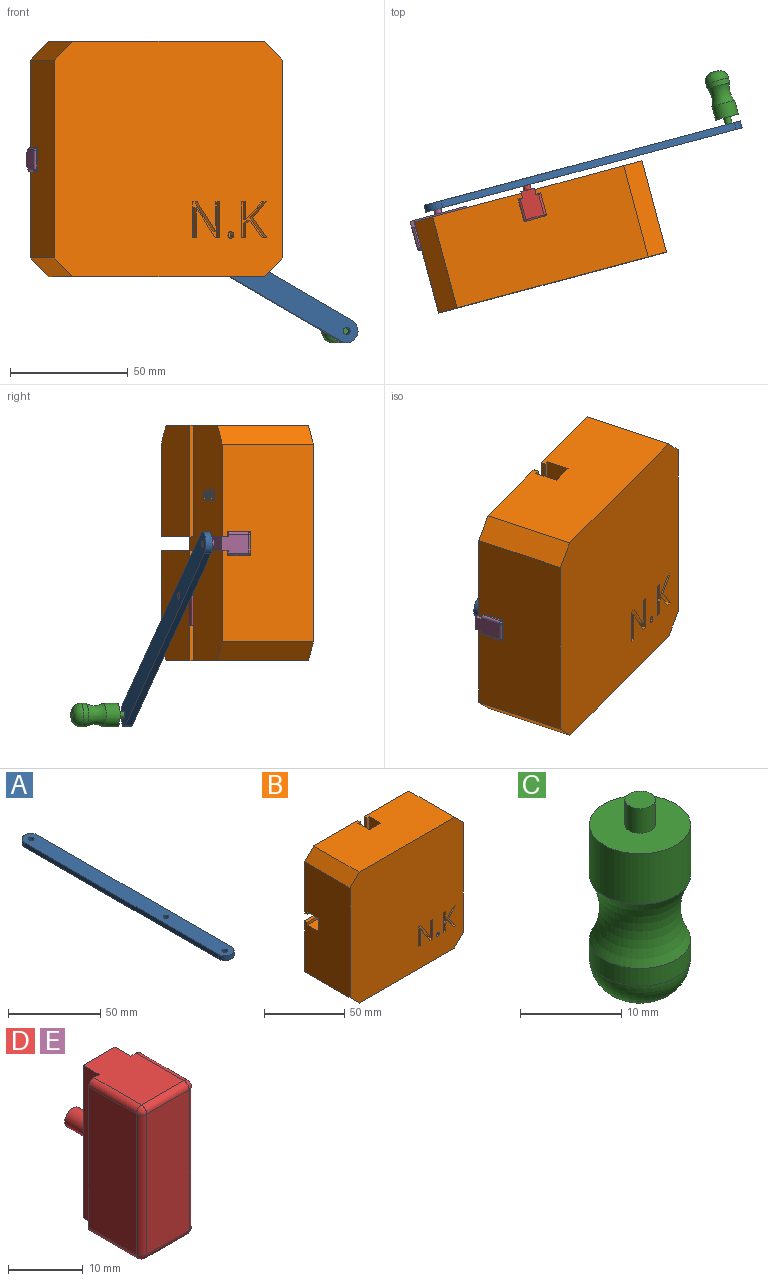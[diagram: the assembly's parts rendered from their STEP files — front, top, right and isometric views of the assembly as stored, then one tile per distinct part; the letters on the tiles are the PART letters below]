
ASSEMBLY  parts=5 mates=6
PART A: 9 faces, bbox 10x158x3 mm
  f0: cylinder r=5mm len=10mm, axis (0,0,-1), area 47.1mm2, adj f1,f6,f7,f8
  f1: plane 148x3mm, normal (-1,0,0), area 444mm2, adj f0,f2,f7,f8
  f2: cylinder r=5mm len=10mm, axis (0,0,-1), area 47.1mm2, adj f1,f6,f7,f8
  f3: cylinder r=1.5mm len=3mm, axis (0,0,-1), area 28.3mm2, adj f7,f8
  f4: cylinder r=1.5mm len=3mm, axis (0,0,-1), area 28.3mm2, adj f7,f8
  f5: cylinder r=1.5mm len=3mm, axis (0,0,-1), area 28.3mm2, adj f7,f8
  f6: plane 148x3mm, normal (1,0,0), area 444mm2, adj f0,f2,f7,f8
  f7: plane 158x10mm, normal (0,0,1), area 1537.3mm2, adj f0,f1,f2,f3,f4,f5,f6
  f8: plane 158x10mm, normal (0,0,-1), area 1537.3mm2, adj f0,f1,f2,f3,f4,f5,f6
PART B: 184 faces, bbox 100x40x100 mm
  f0: plane 47.23x46.91mm, normal (0,1,0), area 2152.4mm2, adj f13,f15,f18,f28,f36,f80,f81,f82
  f1: plane 100x100mm, normal (0,-1,0), area 9730.3mm2, adj f13,f14,f15,f16,f34,f35,f36,f37
  f2: plane 46.91x46.77mm, normal (0,1,0), area 2162.2mm2, adj f4,f14,f15,f27,f35
  f3: plane 47.09x46.77mm, normal (0,1,0), area 2170.2mm2, adj f12,f14,f16,f29,f34
  f4: plane 46.77x2mm, normal (1,0,0), area 93.5mm2, adj f2,f5,f14,f27
  f5: plane 46.77x1.91mm, normal (0,-1,0), area 89.5mm2, adj f4,f6,f14,f27
  f6: plane 46.77x10mm, normal (1,0,0), area 447.5mm2, adj f5,f14,f20,f23,f24,f27
  f7: plane 47.23x10mm, normal (1,0,0), area 453.4mm2, adj f8,f13,f19,f25,f26,f28
  f8: plane 45.3x10mm, normal (0,1,0), area 453mm2, adj f7,f10,f13,f25
  f9: plane 46.77x10mm, normal (-1,0,0), area 447.5mm2, adj f11,f14,f20,f24,f29,f30
  f10: plane 47.23x10mm, normal (-1,0,0), area 453.4mm2, adj f8,f13,f21,f25,f32,f33
  f11: plane 46.77x2.09mm, normal (0,-1,0), area 97.6mm2, adj f9,f12,f14,f29
  f12: plane 46.77x2mm, normal (-1,0,0), area 93.5mm2, adj f3,f11,f14,f29
  f13: plane 84x40mm, normal (0,0,1), area 3248mm2, adj f0,f1,f7,f8,f10,f17,f18,f19
  f14: plane 84x40mm, normal (0,0,-1), area 3248mm2, adj f1,f2,f3,f4,f5,f6,f9,f11
  f15: plane 84x40mm, normal (-1,0,0), area 3246.5mm2, adj f0,f1,f2,f23,f24,f25,f26,f27
  f16: plane 84x40mm, normal (1,0,0), area 3246.5mm2, adj f1,f3,f17,f24,f25,f29,f30,f31
  f17: plane 47.23x47.09mm, normal (0,1,0), area 2191.8mm2, adj f13,f16,f22,f33,f37
  f18: plane 47.23x2mm, normal (1,0,0), area 94.5mm2, adj f0,f13,f19,f28
  f19: plane 47.23x1.91mm, normal (0,-1,0), area 90.4mm2, adj f7,f13,f18,f28
  f20: plane 44.7x10mm, normal (0,1,0), area 447mm2, adj f6,f9,f14,f24
  f21: plane 47.23x2.09mm, normal (0,-1,0), area 98.5mm2, adj f10,f13,f22,f33
  f22: plane 47.23x2mm, normal (-1,0,0), area 94.5mm2, adj f13,f17,f21,f33
  f23: plane 45x2.07mm, normal (0,-1,0), area 93mm2, adj f6,f15,f24,f27
  f24: plane 100x10mm, normal (0,0,1), area 902.5mm2, adj f6,f9,f15,f16,f20,f23,f30,f31
  f25: plane 100x10mm, normal (0,0,-1), area 902.5mm2, adj f7,f8,f10,f15,f16,f26,f31,f32
  f26: plane 45x1.93mm, normal (0,-1,0), area 87mm2, adj f7,f15,f25,f28
  f27: plane 46.91x2.25mm, normal (0,0,1), area 104.9mm2, adj f2,f4,f5,f6,f15,f23
  f28: plane 46.91x2.25mm, normal (0,0,-1), area 104.9mm2, adj f0,f7,f15,f18,f19,f26
  f29: plane 47.09x2.25mm, normal (0,0,1), area 105.2mm2, adj f3,f9,f11,f12,f16,f30
  f30: plane 45x2.07mm, normal (0,-1,0), area 93mm2, adj f9,f16,f24,f29
  f31: plane 100x10mm, normal (0,1,0), area 1000mm2, adj f15,f16,f24,f25
  f32: plane 45x1.93mm, normal (0,-1,0), area 87mm2, adj f10,f16,f25,f33
  f33: plane 47.09x2.25mm, normal (0,0,-1), area 105.2mm2, adj f10,f16,f17,f21,f22,f32
  f34: plane 40x8mm, normal (0.71,0,-0.71), area 452.5mm2, adj f1,f3,f14,f16
  f35: plane 40x8mm, normal (-0.71,0,-0.71), area 452.5mm2, adj f1,f2,f14,f15
  f36: plane 40x8mm, normal (-0.71,0,0.71), area 452.5mm2, adj f0,f1,f13,f15
  f37: plane 40x8mm, normal (0.71,0,0.71), area 452.5mm2, adj f1,f13,f16,f17
  f38: plane 4.6x2.07mm, normal (0,0,1), area 9.5mm2, adj f1,f39,f49,f50
  f39: plane 8.56x6.31mm, normal (-0.8,0,-0.59), area 48.9mm2, adj f1,f38,f40,f50
  f40: plane 6.57x6.08mm, normal (-0.73,0,0.68), area 41.2mm2, adj f1,f39,f41,f50
  f41: plane 4.6x2.08mm, normal (0,0,-1), area 9.6mm2, adj f1,f40,f42,f50
  f42: plane 7.51x6.86mm, normal (0.74,0,-0.67), area 46.8mm2, adj f1,f41,f43,f50
  f43: plane 7.51x4.6mm, normal (-1,0,0), area 34.5mm2, adj f1,f42,f44,f50
  f44: plane 4.6x1.76mm, normal (0,0,-1), area 8.1mm2, adj f1,f43,f45,f50
  f45: plane 15.13x4.6mm, normal (1,0,0), area 69.6mm2, adj f1,f44,f46,f50
  f46: plane 4.6x1.76mm, normal (0,0,1), area 8.1mm2, adj f1,f45,f47,f50
  f47: plane 5.93x4.6mm, normal (-1,0,0), area 27.3mm2, adj f1,f46,f48,f50
  f48: plane 4.6x1.59mm, normal (-0.66,0,0.75), area 9.8mm2, adj f1,f47,f49,f50
  f49: plane 7.34x5.52mm, normal (0.8,0,0.6), area 42.2mm2, adj f1,f38,f48,f50
  f50: plane 15.13x10.93mm, normal (0,-1,0), area 60.4mm2, adj f38,f39,f40,f41,f42,f43,f44,f45
  f51: extruded ~4.6x1.05mm, area 5.2mm2, adj f1,f52,f58,f59
  f52: extruded ~4.6x1.07mm, area 5.3mm2, adj f1,f51,f53,f59
  f53: extruded ~4.6x0.88mm, area 4.4mm2, adj f1,f52,f54,f59
  f54: extruded ~4.6x0.93mm, area 4.7mm2, adj f1,f53,f55,f59
  f55: extruded ~4.6x1.04mm, area 5.1mm2, adj f1,f54,f56,f59
  f56: extruded ~4.6x1.05mm, area 5.2mm2, adj f1,f55,f57,f59
  f57: extruded ~4.6x0.94mm, area 4.7mm2, adj f1,f56,f58,f59
  f58: extruded ~4.6x0.91mm, area 4.6mm2, adj f1,f51,f57,f59
  f59: plane 2.81x2.49mm, normal (0,-1,0), area 5.8mm2, adj f51,f52,f53,f54,f55,f56,f57,f58
  f60: plane 4.6x2.01mm, normal (0,0,1), area 9.2mm2, adj f1,f61,f74,f75
  f61: plane 15.13x4.6mm, normal (-1,0,0), area 69.6mm2, adj f1,f60,f62,f75
  f62: plane 4.6x1.65mm, normal (0,0,-1), area 7.6mm2, adj f1,f61,f63,f75
  f63: plane 8.68x4.6mm, normal (1,0,0), area 39.9mm2, adj f1,f62,f64,f75
  f64: extruded ~4.6x2.17mm, area 10mm2, adj f1,f63,f65,f75
  f65: extruded ~4.6x1.8mm, area 8.3mm2, adj f1,f64,f66,f75
  f66: plane 4.6x0.08mm, normal (0,0,-1), area 0.4mm2, adj f1,f65,f67,f75
  f67: plane 12.65x8.25mm, normal (-0.84,0,-0.55), area 69.5mm2, adj f1,f66,f68,f75
  f68: plane 4.6x1.99mm, normal (0,0,-1), area 9.1mm2, adj f1,f67,f69,f75
  f69: plane 15.13x4.6mm, normal (1,0,0), area 69.6mm2, adj f1,f68,f70,f75
  f70: plane 4.6x1.63mm, normal (0,0,1), area 7.5mm2, adj f1,f69,f71,f75
  f71: plane 8.6x4.6mm, normal (-1,0,0), area 39.6mm2, adj f1,f70,f72,f75
  f72: extruded ~4.6x4.1mm, area 18.9mm2, adj f1,f71,f73,f75
  f73: plane 4.6x0.08mm, normal (0,0,1), area 0.4mm2, adj f1,f72,f74,f75
  f74: plane 12.7x8.27mm, normal (0.84,0,0.55), area 69.7mm2, adj f1,f60,f73,f75
  f75: plane 15.13x11.82mm, normal (0,-1,0), area 75.6mm2, adj f60,f61,f62,f63,f64,f65,f66,f67
  f76: extruded ~23.6x0.68mm, area 17.9mm2, adj f77,f94,f95,f182
  f77: extruded ~23.6x0.65mm, area 17.2mm2, adj f76,f78,f95,f182
  f78: extruded ~23.6x0.78mm, area 19.6mm2, adj f77,f79,f95,f182
  f79: plane 23.6x1.86mm, normal (0,0,-1), area 43.9mm2, adj f78,f94,f95,f182
  f80: extruded ~23.6x1.24mm, area 32.4mm2, adj f0,f81,f93,f95
  f81: extruded ~23.6x0.61mm, area 14.6mm2, adj f0,f80,f82,f95
  f82: extruded ~23.6x0.54mm, area 13.4mm2, adj f0,f81,f83,f95
  f83: plane 23.6x0.48mm, normal (1,0,0), area 11.3mm2, adj f0,f82,f84,f95
  f84: extruded ~23.6x1.14mm, area 27.6mm2, adj f0,f83,f85,f95
  f85: extruded ~23.6x0.85mm, area 22mm2, adj f0,f84,f86,f95
  f86: extruded ~23.6x0.95mm, area 24.2mm2, adj f0,f85,f87,f95
  f87: plane 23.6x2.45mm, normal (0,0,1), area 57.8mm2, adj f0,f86,f88,f95
  f88: plane 23.6x0.34mm, normal (1,0,0), area 8mm2, adj f0,f87,f89,f95
  f89: extruded ~23.6x1.16mm, area 29.6mm2, adj f0,f88,f90,f95
  f90: extruded ~23.6x1.06mm, area 27.9mm2, adj f0,f89,f91,f95
  f91: extruded ~23.6x1.14mm, area 30.4mm2, adj f0,f90,f92,f95
  f92: extruded ~23.6x1.37mm, area 34.5mm2, adj f0,f91,f93,f95
  f93: extruded ~23.6x1.33mm, area 34.1mm2, adj f0,f80,f92,f95
  f94: extruded ~23.6x0.77mm, area 19.9mm2, adj f76,f79,f95,f182
  f95: plane 3.69x3.01mm, normal (0,1,0), area 5mm2, adj f76,f77,f78,f79,f80,f81,f82,f83
  f96: plane 23.6x0.54mm, normal (0,0,1), area 12.7mm2, adj f0,f97,f99,f100
  f97: plane 23.6x5.05mm, normal (1,0,0), area 119.2mm2, adj f0,f96,f98,f100
  f98: plane 23.6x0.54mm, normal (0,0,-1), area 12.7mm2, adj f0,f97,f99,f100
  f99: plane 23.6x5.05mm, normal (-1,0,0), area 119.2mm2, adj f0,f96,f98,f100
  f100: plane 5.05x0.54mm, normal (0,1,0), area 2.7mm2, adj f96,f97,f98,f99
  f101: plane 23.6x2.3mm, normal (-1,0,0), area 54.3mm2, adj f0,f102,f118,f119
  f102: plane 23.6x0.54mm, normal (0,0,1), area 12.7mm2, adj f0,f101,f103,f119
  f103: plane 23.6x2.32mm, normal (1,0,0), area 54.7mm2, adj f0,f102,f104,f119
  f104: extruded ~23.6x0.99mm, area 25.2mm2, adj f0,f103,f105,f119
  f105: extruded ~23.6x0.98mm, area 24.8mm2, adj f0,f104,f106,f119
  f106: extruded ~23.6x0.67mm, area 16.3mm2, adj f0,f105,f107,f119
  f107: extruded ~23.6x0.45mm, area 14.5mm2, adj f0,f106,f108,f119
  f108: plane 23.6x0.03mm, normal (0,0,-1), area 0.8mm2, adj f0,f107,f109,f119
  f109: extruded ~23.6x0.46mm, area 10.8mm2, adj f0,f108,f110,f119
  f110: plane 23.6x1.53mm, normal (1,0,0), area 36.1mm2, adj f0,f109,f111,f119
  f111: plane 23.6x0.54mm, normal (0,0,-1), area 12.7mm2, adj f0,f110,f112,f119
  f112: plane 23.6x5.05mm, normal (-1,0,0), area 119.2mm2, adj f0,f111,f113,f119
  f113: plane 23.6x0.54mm, normal (0,0,1), area 12.7mm2, adj f0,f112,f114,f119
  f114: plane 23.6x1.86mm, normal (1,0,0), area 43.9mm2, adj f0,f113,f115,f119
  f115: extruded ~23.6x1mm, area 24.8mm2, adj f0,f114,f116,f119
  f116: extruded ~23.6x0.82mm, area 21.3mm2, adj f0,f115,f117,f119
  f117: extruded ~23.6x0.62mm, area 15.9mm2, adj f0,f116,f118,f119
  f118: extruded ~23.6x0.65mm, area 16.4mm2, adj f0,f101,f117,f119
  f119: plane 5.05x2.97mm, normal (0,1,0), area 5.4mm2, adj f101,f102,f103,f104,f105,f106,f107,f108
  f120: extruded ~23.6x0.52mm, area 15.8mm2, adj f0,f121,f134,f135
  f121: plane 23.6x0.03mm, normal (0,0,-1), area 0.6mm2, adj f0,f120,f122,f135
  f122: extruded ~23.6x0.55mm, area 13mm2, adj f0,f121,f123,f135
  f123: plane 23.6x2.68mm, normal (1,0,0), area 63.2mm2, adj f0,f122,f124,f135
  f124: plane 23.6x0.53mm, normal (0,0,-1), area 12.6mm2, adj f0,f123,f125,f135
  f125: plane 23.6x5.05mm, normal (-1,0,0), area 119.2mm2, adj f0,f124,f126,f135
  f126: plane 23.6x0.53mm, normal (0,0,1), area 12.6mm2, adj f0,f125,f127,f135
  f127: plane 23.6x1.33mm, normal (1,0,0), area 31.4mm2, adj f0,f126,f128,f135
  f128: plane 23.6x0.41mm, normal (0.65,0,0.76), area 12.6mm2, adj f0,f127,f129,f135
  f129: plane 23.6x1.68mm, normal (-0.8,0,0.6), area 49.5mm2, adj f0,f128,f130,f135
  f130: plane 23.6x0.65mm, normal (0,0,1), area 15.4mm2, adj f0,f129,f131,f135
  f131: plane 23.6x2.04mm, normal (0.8,0,-0.6), area 60.4mm2, adj f0,f130,f132,f135
  f132: plane 23.6x1.52mm, normal (0.72,0,0.69), area 49.3mm2, adj f0,f131,f133,f135
  f133: plane 23.6x0.64mm, normal (0,0,-1), area 15.1mm2, adj f0,f132,f134,f135
  f134: plane 23.6x1.22mm, normal (-0.73,0,-0.69), area 39.5mm2, adj f0,f120,f133,f135
  f135: plane 5.05x2.85mm, normal (0,1,0), area 5.1mm2, adj f120,f121,f122,f123,f124,f125,f126,f127
  f136: extruded ~23.6x0.79mm, area 20.3mm2, adj f137,f162,f163,f183
  f137: extruded ~23.6x0.49mm, area 12.5mm2, adj f136,f138,f163,f183
  f138: extruded ~23.6x0.45mm, area 11.7mm2, adj f137,f139,f163,f183
  f139: extruded ~23.6x0.55mm, area 15.3mm2, adj f138,f140,f163,f183
  f140: extruded ~23.6x0.93mm, area 22.6mm2, adj f139,f141,f163,f183
  f141: plane 23.6x0.54mm, normal (0.04,0,1), area 12.7mm2, adj f140,f142,f163,f183
  f142: plane 23.6x0.32mm, normal (-1,0,0), area 7.6mm2, adj f141,f162,f163,f183
  f143: plane 23.6x0.51mm, normal (-0.98,0,0.21), area 12.2mm2, adj f0,f144,f161,f163
  f144: plane 23.6x0.4mm, normal (0,0,1), area 9.4mm2, adj f0,f143,f145,f163
  f145: plane 23.6x2.43mm, normal (1,0,0), area 57.3mm2, adj f0,f144,f146,f163
  f146: extruded ~23.6x0.91mm, area 23.2mm2, adj f0,f145,f147,f163
  f147: extruded ~23.6x0.94mm, area 23.7mm2, adj f0,f146,f148,f163
  f148: extruded ~23.6x0.63mm, area 15mm2, adj f0,f147,f149,f163
  f149: extruded ~23.6x0.58mm, area 14.6mm2, adj f0,f148,f150,f163
  f150: plane 23.6x0.41mm, normal (-0.93,0,0.37), area 10.5mm2, adj f0,f149,f151,f163
  f151: extruded ~23.6x1.01mm, area 24.8mm2, adj f0,f150,f152,f163
  f152: extruded ~23.6x0.58mm, area 14.8mm2, adj f0,f151,f153,f163
  f153: extruded ~23.6x0.62mm, area 15.5mm2, adj f0,f152,f154,f163
  f154: plane 23.6x0.22mm, normal (-1,0,0), area 5.2mm2, adj f0,f153,f155,f163
  f155: plane 23.6x0.6mm, normal (-0.03,0,-1), area 14.2mm2, adj f0,f154,f156,f163
  f156: extruded ~23.6x1.72mm, area 54.6mm2, adj f0,f155,f157,f163
  f157: extruded ~23.6x0.78mm, area 20.2mm2, adj f0,f156,f158,f163
  f158: extruded ~23.6x0.83mm, area 21.1mm2, adj f0,f157,f159,f163
  f159: extruded ~23.6x0.66mm, area 16mm2, adj f0,f158,f160,f163
  f160: extruded ~23.6x0.53mm, area 16.6mm2, adj f0,f159,f161,f163
  f161: plane 23.6x0.03mm, normal (0,0,1), area 0.6mm2, adj f0,f143,f160,f163
  f162: extruded ~23.6x0.77mm, area 20mm2, adj f136,f142,f163,f183
  f163: plane 3.68x2.85mm, normal (0,1,0), area 5mm2, adj f136,f137,f138,f139,f140,f141,f142,f143
  f164: plane 23.6x2.3mm, normal (-1,0,0), area 54.3mm2, adj f0,f165,f180,f181
  f165: plane 23.6x0.54mm, normal (0,0,1), area 12.7mm2, adj f0,f164,f166,f181
  f166: plane 23.6x2.32mm, normal (1,0,0), area 54.7mm2, adj f0,f165,f167,f181
  f167: extruded ~23.6x0.99mm, area 25.3mm2, adj f0,f166,f168,f181
  f168: extruded ~23.6x0.97mm, area 24.6mm2, adj f0,f167,f169,f181
  f169: extruded ~23.6x0.67mm, area 16.2mm2, adj f0,f168,f170,f181
  f170: extruded ~23.6x0.46mm, area 14.8mm2, adj f0,f169,f171,f181
  f171: plane 23.6x0.03mm, normal (0,0,-1), area 0.6mm2, adj f0,f170,f172,f181
  f172: plane 23.6x0.49mm, normal (0.98,0,-0.18), area 11.7mm2, adj f0,f171,f173,f181
  f173: plane 23.6x0.44mm, normal (0,0,-1), area 10.3mm2, adj f0,f172,f174,f181
  f174: plane 23.6x3.56mm, normal (-1,0,0), area 83.9mm2, adj f0,f173,f175,f181
  f175: plane 23.6x0.54mm, normal (0,0,1), area 12.7mm2, adj f0,f174,f176,f181
  f176: plane 23.6x1.87mm, normal (1,0,0), area 44mm2, adj f0,f175,f177,f181
  f177: extruded ~23.6x1mm, area 24.8mm2, adj f0,f176,f178,f181
  f178: extruded ~23.6x0.82mm, area 21.2mm2, adj f0,f177,f179,f181
  f179: extruded ~23.6x0.62mm, area 15.9mm2, adj f0,f178,f180,f181
  f180: extruded ~23.6x0.65mm, area 16.4mm2, adj f0,f164,f179,f181
  f181: plane 3.62x2.97mm, normal (0,1,0), area 4.6mm2, adj f164,f165,f166,f167,f168,f169,f170,f171
  f182: plane 1.86x1.05mm, normal (0,1,0), area 1.6mm2, adj f76,f77,f78,f79,f94
  f183: plane 1.75x1.37mm, normal (0,1,0), area 1.9mm2, adj f136,f137,f138,f139,f140,f141,f142,f162
PART C: 8 faces, bbox 13.7x13.7x23 mm
  f0: plane 2x2mm, normal (0,0,-1), area 3.1mm2, adj f1
  f1: torus R=1mm, axis (0,0,-1), area 140mm2, adj f0,f2
  f2: cylinder r=5mm len=10mm, axis (0,0,-1), area 66.8mm2, adj f1,f3
  f3: torus R=12mm, axis (0,0,-1), area 220.3mm2, adj f2,f4
  f4: cylinder r=5mm len=10mm, axis (0,0,-1), area 192.5mm2, adj f3,f5
  f5: plane 10x10mm, normal (0,0,1), area 71.5mm2, adj f4,f6
  f6: cylinder r=1.5mm len=3mm, axis (0,0,-1), area 28.3mm2, adj f5,f7
  f7: plane 3x3mm, normal (0,0,1), area 7.1mm2, adj f6
PART D: 24 faces, bbox 10x18x25 mm
  f0: plane 25x3mm, normal (-1,0,0), area 75mm2, adj f1,f7,f8,f9
  f1: plane 25x2mm, normal (0,1,0), area 49.6mm2, adj f0,f2,f8,f9,f17,f20
  f2: plane 23x9mm, normal (-1,0,0), area 207mm2, adj f1,f17,f20,f23
  f3: plane 23x8mm, normal (0,-1,0), area 184mm2, adj f13,f18,f19,f23
  f4: plane 23x9mm, normal (1,0,0), area 207mm2, adj f5,f12,f13,f14
  f5: plane 25x2mm, normal (0,1,0), area 49.6mm2, adj f4,f6,f8,f9,f12,f14
  f6: plane 25x3mm, normal (1,0,0), area 75mm2, adj f5,f7,f8,f9
  f7: plane 25x6mm, normal (0,1,0), area 142.9mm2, adj f0,f6,f8,f9,f10
  f8: plane 12x8mm, normal (0,0,1), area 90mm2, adj f0,f1,f5,f6,f7,f12,f17,f18
  f9: plane 12x8mm, normal (0,0,-1), area 90mm2, adj f0,f1,f5,f6,f7,f14,f19,f20
  f10: cylinder r=1.5mm len=5mm, axis (0,-1,0), area 47.1mm2, adj f7,f11
  f11: plane 3x3mm, normal (0,1,0), area 7.1mm2, adj f10
  f12: cylinder r=1mm len=9mm, axis (0,-1,0), area 14.1mm2, adj f4,f5,f8,f15
  f13: cylinder r=1mm len=23mm, axis (0,0,-1), area 36.1mm2, adj f3,f4,f15,f16
  f14: cylinder r=1mm len=9mm, axis (0,1,0), area 14.1mm2, adj f4,f5,f9,f16
  f15: sphere r=1mm, area 1.6mm2, adj f12,f13,f18
  f16: sphere r=1mm, area 1.6mm2, adj f13,f14,f19
  f17: cylinder r=1mm len=9mm, axis (0,1,0), area 14.1mm2, adj f1,f2,f8,f21
  f18: cylinder r=1mm len=8mm, axis (-1,0,0), area 12.6mm2, adj f3,f8,f15,f21
  f19: cylinder r=1mm len=8mm, axis (1,0,0), area 12.6mm2, adj f3,f9,f16,f22
  f20: cylinder r=1mm len=9mm, axis (0,-1,0), area 14.1mm2, adj f1,f2,f9,f22
  f21: sphere r=1mm, area 1.6mm2, adj f17,f18,f23
  f22: sphere r=1mm, area 1.6mm2, adj f19,f20,f23
  f23: cylinder r=1mm len=23mm, axis (0,0,1), area 36.1mm2, adj f2,f3,f21,f22
PART E: same geometry as D
PLACE A rot(axis=(-0.74,-0.57,-0.36),98.6deg) t=(-318.21,-165.71,23.25)mm
PLACE B rot(axis=(0,0,1),15deg) t=(-247.14,-149.52,75.08)mm fixed
PLACE C rot(axis=(0.3,0.72,-0.62),128.6deg) t=(-232.85,-75.39,41.1)mm
PLACE D rot(axis=(0,0,1),15deg) t=(-259.72,-221.98,47.47)mm
PLACE E rot(axis=(0.13,-0.98,0.13),91deg) t=(-256.11,-221.02,51.64)mm
MATE fastened A.f0 <-> C.f1  axis (-0.26,0.97,0) through (-162.42,-120.86,9.38)mm
MATE planar E.f2 <-> B.f24  axis (0,0,-1) through (-283.71,-166.3,77.07)mm
MATE revolute A.f2 <-> E.f10  axis (-0.26,0.97,0) through (-286.95,-154.23,82.07)mm
MATE planar D.f2 <-> B.f6  axis (-0.97,-0.26,0) through (-250.68,-157.45,59.97)mm
MATE revolute D.f10 <-> A.f5  axis (-0.26,0.97,0) through (-249.09,-144.08,59.97)mm
MATE planar E.f10 <-> B.f31  axis (0.26,-0.97,0) through (-282.29,-171.61,82.07)mm
